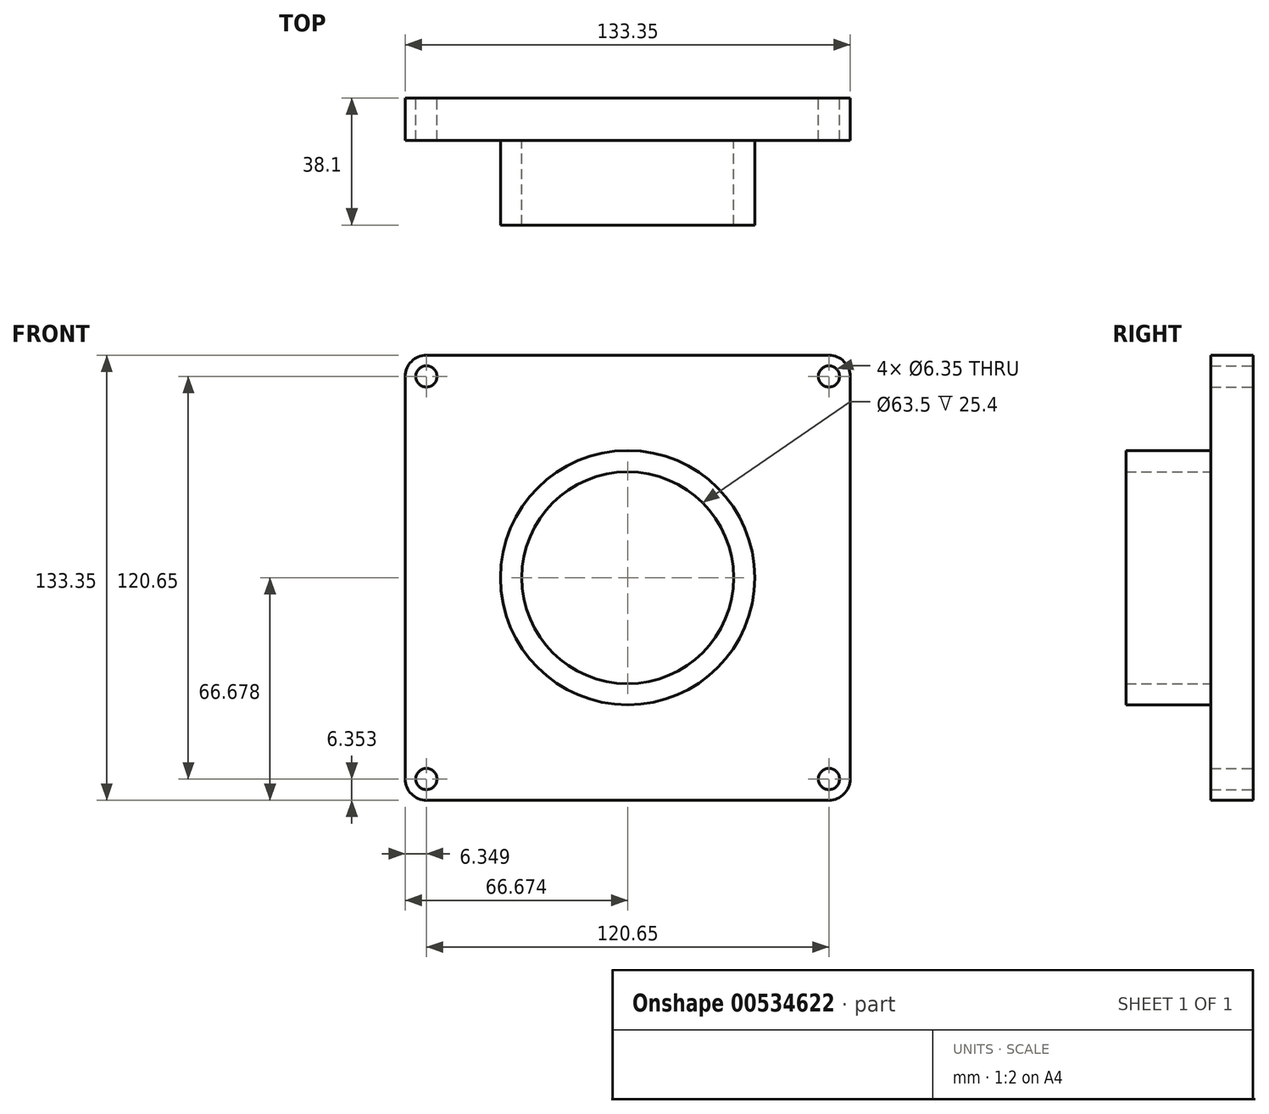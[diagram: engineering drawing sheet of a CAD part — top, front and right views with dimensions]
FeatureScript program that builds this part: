
annotation { "Feature Type Name" : "Feature", "Feature Type Description" : "" }
export const myFeature = defineFeature(function(context is Context, id is Id, definition is map)
    precondition{}
    {
        {
            var Q0;
            Q0=qCreatedBy(makeId("Front.planeOp"),FACE);
            var sketch = newSketch(context, id + "F0", { "sketchPlane" : qUnion([Q0])});
            skLineSegment(sketch, "E0.bottom", {"start": v(-53.05, 64) * mm, "end": v(67.6, 64) * mm});
            skLineSegment(sketch, "E0.top", {"start": v(-53.05, -69.36) * mm, "end": v(67.6, -69.36) * mm});
            skLineSegment(sketch, "E0.left", {"start": v(-59.4, 57.64) * mm, "end": v(-59.4, -63) * mm});
            skLineSegment(sketch, "E0.right", {"start": v(73.95, 57.64) * mm, "end": v(73.95, -63) * mm});
            skPoint(sketch, "E1.visualSharp", {"position": v(-59.4, 64) * mm});
            skArc(sketch, "E1.filletArc", {"start": v(-53.05, 64) * mm, "mid": v(-57.54, 62.13) * mm, "end": v(-59.4, 57.64) * mm});
            skPoint(sketch, "E2.visualSharp", {"position": v(73.95, 64) * mm});
            skArc(sketch, "E2.filletArc", {"start": v(73.95, 57.64) * mm, "mid": v(72.09, 62.13) * mm, "end": v(67.6, 64) * mm});
            skPoint(sketch, "E3.visualSharp", {"position": v(73.95, -69.36) * mm});
            skArc(sketch, "E3.filletArc", {"start": v(67.6, -69.36) * mm, "mid": v(72.09, -67.5) * mm, "end": v(73.95, -63) * mm});
            skPoint(sketch, "E4.visualSharp", {"position": v(-59.4, -69.36) * mm});
            skArc(sketch, "E4.filletArc", {"start": v(-59.4, -63) * mm, "mid": v(-57.54, -67.5) * mm, "end": v(-53.05, -69.36) * mm});
            skCircle(sketch, "E5", {"center": v(67.6, 57.64) * mm, "radius": 3.18 * mm});
            skCircle(sketch, "E6", {"center": v(67.6, -63) * mm, "radius": 3.18 * mm});
            skCircle(sketch, "E7", {"center": v(-53.05, -63) * mm, "radius": 3.18 * mm});
            skCircle(sketch, "E8", {"center": v(-53.05, 57.64) * mm, "radius": 3.17 * mm});
            skSolve(sketch);
        }
        {
            var Q0;
            Q0=makeQuery(id+"F0.imprint","IMPRINT",FACE,{"disambiguationData":[TD([[makeQuery(id+"F0.imprint","IMPRINT",EDGE,{"derivedFrom":sQuery(id+"F0.wireOp",EDGE,"E0.bottom")}),-1.0]])]});
            extrude(context, id + "F1", {"entities" : qUnion([Q0]), "depth" : 12.7 * mm, "offsetDistance" : 25.4 * mm});
        }
        {
            var Q0;
            Q0=makeQuery(id+"F1.opExtrude","CAP_FACE",FACE,{"disambiguationData":[OSD([sQuery(id+"F0.wireOp",EDGE,"E0.bottom"),sQuery(id+"F0.wireOp",EDGE,"E0.top"),sQuery(id+"F0.wireOp",EDGE,"E0.left"),sQuery(id+"F0.wireOp",EDGE,"E0.right"),sQuery(id+"F0.wireOp",EDGE,"E1.filletArc"),sQuery(id+"F0.wireOp",EDGE,"E2.filletArc"),sQuery(id+"F0.wireOp",EDGE,"E3.filletArc"),sQuery(id+"F0.wireOp",EDGE,"E4.filletArc"),sQuery(id+"F0.wireOp",EDGE,"E5"),sQuery(id+"F0.wireOp",EDGE,"E6"),sQuery(id+"F0.wireOp",EDGE,"E7"),sQuery(id+"F0.wireOp",EDGE,"E8")])],"isStart":false});
            var sketch = newSketch(context, id + "F2", { "sketchPlane" : qUnion([Q0])});
            skPoint(sketch, "E9", {"position": v(7.27, -2.68) * mm});
            skCircle(sketch, "E10", {"center": v(7.27, -2.68) * mm, "radius": 38.1 * mm});
            skCircle(sketch, "E11", {"center": v(7.27, -2.68) * mm, "radius": 31.75 * mm});
            skSolve(sketch);
        }
        {
            var Q0;
            Q0=makeQuery(id+"F2.imprint","IMPRINT",FACE,{"disambiguationData":[TD([[makeQuery(id+"F2.imprint","IMPRINT",EDGE,{"derivedFrom":sQuery(id+"F2.wireOp",EDGE,"E10")}),1.0]])]});
            extrude(context, id + "F3", {"entities" : qUnion([Q0]), "operationType" : NewBodyOperationType.ADD, "depth" : 25.4 * mm, "offsetDistance" : 25.4 * mm});
        }
    });
